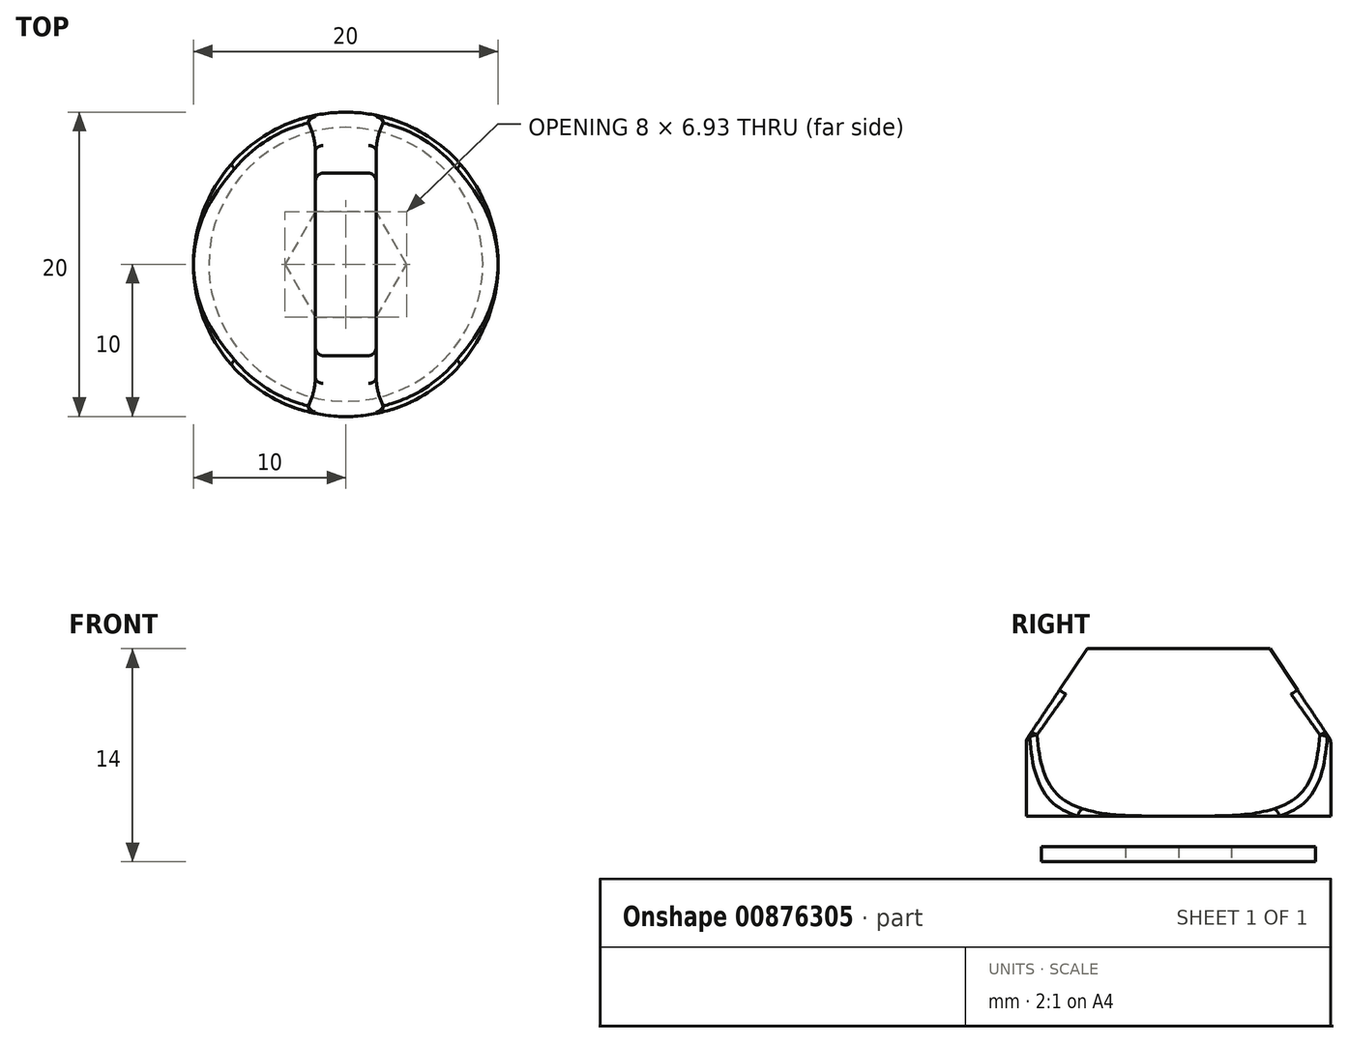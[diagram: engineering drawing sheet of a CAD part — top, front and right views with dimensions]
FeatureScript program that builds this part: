
annotation { "Feature Type Name" : "Feature", "Feature Type Description" : "" }
export const myFeature = defineFeature(function(context is Context, id is Id, definition is map)
    precondition{}
    {
        {
            var Q0;
            Q0=qCreatedBy(makeId("Top.planeOp"),FACE);
            var sketch = newSketch(context, id + "F0", { "sketchPlane" : qUnion([Q0])});
            skCircle(sketch, "E0", {"center": v(0, 0) * mm, "radius": 10 * mm});
            skCircle(sketch, "E1", {"center": v(0, 0) * mm, "radius": 9 * mm});
            skSolve(sketch);
        }
        {
            var Q0;
            Q0=makeQuery(id+"F0.imprint","IMPRINT",FACE,{"disambiguationData":[TD([[makeQuery(id+"F0.imprint","IMPRINT",EDGE,{"derivedFrom":sQuery(id+"F0.wireOp",EDGE,"E1")}),1.0]])]});
            var Q1;
            Q1=makeQuery(id+"F0.imprint","IMPRINT",FACE,{"disambiguationData":[TD([[makeQuery(id+"F0.imprint","IMPRINT",EDGE,{"derivedFrom":sQuery(id+"F0.wireOp",EDGE,"E0")}),1.0]])]});
            extrude(context, id + "F1", {"entities" : qUnion([Q0, Q1]), "depth" : 13 * mm, "offsetDistance" : 25 * mm});
        }
        {
            var Q0;
            Q0=makeQuery(id+"F0.imprint","IMPRINT",FACE,{"disambiguationData":[TD([[makeQuery(id+"F0.imprint","IMPRINT",EDGE,{"derivedFrom":sQuery(id+"F0.wireOp",EDGE,"E1")}),1.0]])]});
            extrude(context, id + "F2", {"entities" : qUnion([Q0]), "operationType" : NewBodyOperationType.ADD, "oppositeDirection" : true, "depth" : 1 * mm, "offsetDistance" : 25 * mm});
        }
        {
            var Q0;
            Q0=qCreatedBy(makeId("Front.planeOp"),FACE);
            var sketch = newSketch(context, id + "F3", { "sketchPlane" : qUnion([Q0])});
            skLineSegment(sketch, "E2.bottom", {"start": v(0, 0) * mm, "end": v(10, 0) * mm});
            skLineSegment(sketch, "E2.top", {"start": v(0, 13) * mm, "end": v(10, 13) * mm});
            skLineSegment(sketch, "E2.left", {"start": v(0, 0) * mm, "end": v(0, 13) * mm});
            skLineSegment(sketch, "E2.right", {"start": v(10, 0) * mm, "end": v(10, 13) * mm});
            skLineSegment(sketch, "E3.bottom", {"start": v(0, 0) * mm, "end": v(-10, 0) * mm});
            skLineSegment(sketch, "E3.top", {"start": v(0, 13) * mm, "end": v(-10, 13) * mm});
            skLineSegment(sketch, "E3.right", {"start": v(-10, 0) * mm, "end": v(-10, 13) * mm});
            skLineSegment(sketch, "E4.bottom", {"start": v(-10, 0) * mm, "end": v(10, 0) * mm});
            skLineSegment(sketch, "E4.top", {"start": v(-10, 2) * mm, "end": v(10, 2) * mm});
            skLineSegment(sketch, "E4.left", {"start": v(-10, 0) * mm, "end": v(-10, 2) * mm});
            skLineSegment(sketch, "E4.right", {"start": v(10, 0) * mm, "end": v(10, 2) * mm});
            skArc(sketch, "E5", {"start": v(2, 10) * mm, "mid": v(4.34, 4.34) * mm, "end": v(10, 2) * mm});
            skPoint(sketch, "E5.centerSnap0", {"position": v(10, 6.5) * mm});
            skArc(sketch, "E6", {"start": v(-10, 2) * mm, "mid": v(-4.34, 4.34) * mm, "end": v(-2, 10) * mm});
            skLineSegment(sketch, "E7", {"start": v(-2, 10) * mm, "end": v(-2, 13) * mm});
            skLineSegment(sketch, "E8", {"start": v(2, 10) * mm, "end": v(2, 13) * mm});
            skSolve(sketch);
        }
        {
            var Q0;
            {var subQ0=sQuery(id+"F3.wireOp",EDGE,"E3.right");Q0=makeQuery(id+"F3.imprint","IMPRINT",FACE,{"disambiguationData":[TD([[makeQuery(id+"F3.imprint","IMPRINT",EDGE,{"derivedFrom":subQ0}),-1.0]])]});}
            var Q1;
            {var subQ0=sQuery(id+"F3.wireOp",EDGE,"E2.right");Q1=makeQuery(id+"F3.imprint","IMPRINT",FACE,{"disambiguationData":[TD([[makeQuery(id+"F3.imprint","IMPRINT",EDGE,{"derivedFrom":subQ0}),1.0]])]});}
            extrude(context, id + "F4", {"entities" : qUnion([Q0, Q1]), "operationType" : NewBodyOperationType.REMOVE, "endBound" : BoundingType.SYMMETRIC, "oppositeDirection" : true, "depth" : 25 * mm, "offsetDistance" : 25 * mm});
        }
        {
            var Q0;
            Q0=qCreatedBy(makeId("Right.planeOp"),FACE);
            var sketch = newSketch(context, id + "F5", { "sketchPlane" : qUnion([Q0])});
            skLineSegment(sketch, "E9.bottom", {"start": v(0, 0) * mm, "end": v(10, 0) * mm});
            skLineSegment(sketch, "E9.top", {"start": v(0, 7) * mm, "end": v(10, 7) * mm});
            skLineSegment(sketch, "E9.left", {"start": v(0, 0) * mm, "end": v(0, 7) * mm});
            skLineSegment(sketch, "E9.right", {"start": v(10, 0) * mm, "end": v(10, 7) * mm});
            skLineSegment(sketch, "E10", {"start": v(0, 7) * mm, "end": v(0, 13) * mm});
            skLineSegment(sketch, "E11.bottom", {"start": v(0, 13) * mm, "end": v(6, 13) * mm});
            skLineSegment(sketch, "E11.top", {"start": v(0, 7) * mm, "end": v(6, 7) * mm});
            skLineSegment(sketch, "E11.left", {"start": v(0, 13) * mm, "end": v(0, 7) * mm});
            skLineSegment(sketch, "E11.right", {"start": v(6, 13) * mm, "end": v(6, 7) * mm});
            skLineSegment(sketch, "E12.bottom", {"start": v(0, 13) * mm, "end": v(-6, 13) * mm});
            skLineSegment(sketch, "E12.top", {"start": v(0, 7) * mm, "end": v(-6, 7) * mm});
            skLineSegment(sketch, "E12.right", {"start": v(-6, 13) * mm, "end": v(-6, 7) * mm});
            skLineSegment(sketch, "E13", {"start": v(6, 13) * mm, "end": v(10, 7) * mm});
            skLineSegment(sketch, "E14.bottom", {"start": v(0, 7) * mm, "end": v(-10, 7) * mm});
            skLineSegment(sketch, "E14.top", {"start": v(0, 0) * mm, "end": v(-10, 0) * mm});
            skLineSegment(sketch, "E14.left", {"start": v(0, 7) * mm, "end": v(0, 0) * mm});
            skLineSegment(sketch, "E14.right", {"start": v(-10, 7) * mm, "end": v(-10, 0) * mm});
            skLineSegment(sketch, "E15", {"start": v(-10, 7) * mm, "end": v(-6, 13) * mm});
            skLineSegment(sketch, "E16.bottom", {"start": v(-6, 7) * mm, "end": v(-10, 7) * mm});
            skLineSegment(sketch, "E16.top", {"start": v(-6, 13) * mm, "end": v(-10, 13) * mm});
            skLineSegment(sketch, "E16.left", {"start": v(-6, 7) * mm, "end": v(-6, 13) * mm});
            skLineSegment(sketch, "E16.right", {"start": v(-10, 7) * mm, "end": v(-10, 13) * mm});
            skLineSegment(sketch, "E17.bottom", {"start": v(6, 13) * mm, "end": v(10, 13) * mm});
            skLineSegment(sketch, "E17.top", {"start": v(6, 7) * mm, "end": v(10, 7) * mm});
            skLineSegment(sketch, "E17.right", {"start": v(10, 13) * mm, "end": v(10, 7) * mm});
            skSolve(sketch);
        }
        {
            var Q0;
            Q0=makeQuery(id+"F5.imprint","IMPRINT",FACE,{"disambiguationData":[TD([[makeQuery(id+"F5.imprint","IMPRINT",EDGE,{"derivedFrom":sQuery(id+"F5.wireOp",EDGE,"E15")}),1.0]])]});
            var Q1;
            Q1=makeQuery(id+"F5.imprint","IMPRINT",FACE,{"disambiguationData":[TD([[makeQuery(id+"F5.imprint","IMPRINT",EDGE,{"derivedFrom":sQuery(id+"F5.wireOp",EDGE,"E13")}),1.0]])]});
            extrude(context, id + "F6", {"entities" : qUnion([Q0, Q1]), "operationType" : NewBodyOperationType.REMOVE, "endBound" : BoundingType.SYMMETRIC, "oppositeDirection" : true, "depth" : 25 * mm, "offsetDistance" : 25 * mm});
        }
        {
            var Q0;
            Q0=makeQuery(id+"F4.boolean.opBoolean","COPY",EDGE,{"derivedFrom":makeQuery(id+"F4.opExtrude","SWEPT_EDGE",EDGE,{"disambiguationData":[OSD([sQuery(id+"F3.wireOp",EDGE,"E3.top"),sQuery(id+"F3.wireOp",EDGE,"E7")])]})});
            var Q1;
            Q1=makeQuery(id+"F4.boolean.opBoolean","COPY",EDGE,{"derivedFrom":makeQuery(id+"F4.opExtrude","SWEPT_EDGE",EDGE,{"disambiguationData":[OSD([sQuery(id+"F3.wireOp",EDGE,"E2.top"),sQuery(id+"F3.wireOp",EDGE,"E8")])]})});
            var Q2;
            Q2=makeQuery(id+"F6.boolean.opBoolean","COPY",EDGE,{"derivedFrom":makeQuery(id+"F6.opExtrude","SWEPT_EDGE",EDGE,{"disambiguationData":[OSD([sQuery(id+"F5.wireOp",EDGE,"E12.bottom"),sQuery(id+"F5.wireOp",EDGE,"E15"),sQuery(id+"F5.wireOp",EDGE,"E16.top"),sQuery(id+"F5.wireOp",EDGE,"E16.left")])]})});
            var Q3;
            Q3=makeQuery(id+"F6.boolean.opBoolean","INTERSECT",EDGE,{"derivedFrom":[makeQuery(id+"F4.boolean.opBoolean","COPY",FACE,{"derivedFrom":makeQuery(id+"F4.opExtrude","SWEPT_FACE",FACE,{"disambiguationData":[OSD([sQuery(id+"F3.wireOp",EDGE,"E8")])]})}),makeQuery(id+"F6.opExtrude","SWEPT_FACE",FACE,{"disambiguationData":[OSD([sQuery(id+"F5.wireOp",EDGE,"E15")])]})]});
            var Q4;
            Q4=makeQuery(id+"F6.boolean.opBoolean","INTERSECT",EDGE,{"derivedFrom":[makeQuery(id+"F4.boolean.opBoolean","COPY",FACE,{"derivedFrom":makeQuery(id+"F4.opExtrude","SWEPT_FACE",FACE,{"disambiguationData":[OSD([sQuery(id+"F3.wireOp",EDGE,"E7")])]})}),makeQuery(id+"F6.opExtrude","SWEPT_FACE",FACE,{"disambiguationData":[OSD([sQuery(id+"F5.wireOp",EDGE,"E15")])]})]});
            var Q5;
            Q5=makeQuery(id+"F6.boolean.opBoolean","INTERSECT",EDGE,{"derivedFrom":[makeQuery(id+"F4.boolean.opBoolean","COPY",FACE,{"derivedFrom":makeQuery(id+"F4.opExtrude","SWEPT_FACE",FACE,{"disambiguationData":[OSD([sQuery(id+"F3.wireOp",EDGE,"E5")])]})}),makeQuery(id+"F6.opExtrude","SWEPT_FACE",FACE,{"disambiguationData":[OSD([sQuery(id+"F5.wireOp",EDGE,"E15")])]})]});
            var Q6;
            Q6=makeQuery(id+"F6.boolean.opBoolean","INTERSECT",EDGE,{"derivedFrom":[makeQuery(id+"F4.boolean.opBoolean","COPY",FACE,{"derivedFrom":makeQuery(id+"F4.opExtrude","SWEPT_FACE",FACE,{"disambiguationData":[OSD([sQuery(id+"F3.wireOp",EDGE,"E6")])]})}),makeQuery(id+"F6.opExtrude","SWEPT_FACE",FACE,{"disambiguationData":[OSD([sQuery(id+"F5.wireOp",EDGE,"E15")])]})]});
            var Q7;
            Q7=makeQuery(id+"F6.boolean.opBoolean","INTERSECT",EDGE,{"derivedFrom":[makeQuery(id+"F1.opExtrude","SWEPT_FACE",FACE,{"disambiguationData":[OSD([sQuery(id+"F0.wireOp",EDGE,"E0")])]}),makeQuery(id+"F6.opExtrude","SWEPT_FACE",FACE,{"disambiguationData":[OSD([sQuery(id+"F5.wireOp",EDGE,"E15")])]})]});
            var Q8;
            Q8=makeQuery(id+"F6.boolean.opBoolean","COPY",EDGE,{"derivedFrom":makeQuery(id+"F6.opExtrude","SWEPT_EDGE",EDGE,{"disambiguationData":[OSD([sQuery(id+"F5.wireOp",EDGE,"E11.bottom"),sQuery(id+"F5.wireOp",EDGE,"E13"),sQuery(id+"F5.wireOp",EDGE,"E17.bottom"),sQuery(id+"F5.wireOp",EDGE,"E11.right")])]})});
            var Q9;
            Q9=makeQuery(id+"F6.boolean.opBoolean","INTERSECT",EDGE,{"derivedFrom":[makeQuery(id+"F4.boolean.opBoolean","COPY",FACE,{"derivedFrom":makeQuery(id+"F4.opExtrude","SWEPT_FACE",FACE,{"disambiguationData":[OSD([sQuery(id+"F3.wireOp",EDGE,"E7")])]})}),makeQuery(id+"F6.opExtrude","SWEPT_FACE",FACE,{"disambiguationData":[OSD([sQuery(id+"F5.wireOp",EDGE,"E13")])]})]});
            var Q10;
            Q10=makeQuery(id+"F6.boolean.opBoolean","INTERSECT",EDGE,{"derivedFrom":[makeQuery(id+"F4.boolean.opBoolean","COPY",FACE,{"derivedFrom":makeQuery(id+"F4.opExtrude","SWEPT_FACE",FACE,{"disambiguationData":[OSD([sQuery(id+"F3.wireOp",EDGE,"E6")])]})}),makeQuery(id+"F6.opExtrude","SWEPT_FACE",FACE,{"disambiguationData":[OSD([sQuery(id+"F5.wireOp",EDGE,"E13")])]})]});
            var Q11;
            Q11=makeQuery(id+"F6.boolean.opBoolean","INTERSECT",EDGE,{"derivedFrom":[makeQuery(id+"F4.boolean.opBoolean","COPY",FACE,{"derivedFrom":makeQuery(id+"F4.opExtrude","SWEPT_FACE",FACE,{"disambiguationData":[OSD([sQuery(id+"F3.wireOp",EDGE,"E5")])]})}),makeQuery(id+"F6.opExtrude","SWEPT_FACE",FACE,{"disambiguationData":[OSD([sQuery(id+"F5.wireOp",EDGE,"E13")])]})]});
            var Q12;
            Q12=makeQuery(id+"F6.boolean.opBoolean","INTERSECT",EDGE,{"derivedFrom":[makeQuery(id+"F4.boolean.opBoolean","COPY",FACE,{"derivedFrom":makeQuery(id+"F4.opExtrude","SWEPT_FACE",FACE,{"disambiguationData":[OSD([sQuery(id+"F3.wireOp",EDGE,"E8")])]})}),makeQuery(id+"F6.opExtrude","SWEPT_FACE",FACE,{"disambiguationData":[OSD([sQuery(id+"F5.wireOp",EDGE,"E13")])]})]});
            var Q13;
            Q13=makeQuery(id+"F6.boolean.opBoolean","INTERSECT",EDGE,{"derivedFrom":[makeQuery(id+"F1.opExtrude","SWEPT_FACE",FACE,{"disambiguationData":[OSD([sQuery(id+"F0.wireOp",EDGE,"E0")])]}),makeQuery(id+"F6.opExtrude","SWEPT_FACE",FACE,{"disambiguationData":[OSD([sQuery(id+"F5.wireOp",EDGE,"E13")])]})]});
            var Q14;
            Q14=makeQuery(id+"F4.boolean.opBoolean","INTERSECT",EDGE,{"derivedFrom":[makeQuery(id+"F1.opExtrude","SWEPT_FACE",FACE,{"disambiguationData":[OSD([sQuery(id+"F0.wireOp",EDGE,"E0")])]}),makeQuery(id+"F4.opExtrude","SWEPT_FACE",FACE,{"disambiguationData":[OSD([sQuery(id+"F3.wireOp",EDGE,"E5")])]})]});
            var Q15;
            Q15=makeQuery(id+"F4.boolean.opBoolean","INTERSECT",EDGE,{"derivedFrom":[makeQuery(id+"F1.opExtrude","SWEPT_FACE",FACE,{"disambiguationData":[OSD([sQuery(id+"F0.wireOp",EDGE,"E0")])]}),makeQuery(id+"F4.opExtrude","SWEPT_FACE",FACE,{"disambiguationData":[OSD([sQuery(id+"F3.wireOp",EDGE,"E6")])]})]});
            fillet(context, id + "F7", {"entities" : qUnion([Q0, Q1, Q2, Q3, Q4, Q5, Q6, Q7, Q8, Q9, Q10, Q11, Q12, Q13, Q14, Q15]), "radius" : 0.5 * mm, "tangentPropagation" : true, "allowEdgeOverflow" : false});
        }
        {
            var Q0;
            Q0=makeQuery(id+"F2.opExtrude","CAP_FACE",FACE,{"disambiguationData":[OSD([sQuery(id+"F0.wireOp",EDGE,"E1")])],"isStart":false});
            var sketch = newSketch(context, id + "F8", { "sketchPlane" : qUnion([Q0])});
            skCircle(sketch, "E18", {"center": v(0, 0) * mm, "radius": 4 * mm});
            skCircle(sketch, "E19.cCircle", {"center": v(0, 0) * mm, "radius": 4 * mm, "construction": true});
            skLineSegment(sketch, "E19.0", {"start": v(4, 0) * mm, "end": v(2, -3.46) * mm});
            skLineSegment(sketch, "E19.1", {"start": v(2, -3.46) * mm, "end": v(-2, -3.46) * mm});
            skLineSegment(sketch, "E19.2", {"start": v(-2, -3.46) * mm, "end": v(-4, 0) * mm});
            skLineSegment(sketch, "E19.3", {"start": v(-4, 0) * mm, "end": v(-2, 3.46) * mm});
            skLineSegment(sketch, "E19.4", {"start": v(-2, 3.46) * mm, "end": v(2, 3.46) * mm});
            skLineSegment(sketch, "E19.5", {"start": v(2, 3.46) * mm, "end": v(4, 0) * mm});
            skSolve(sketch);
        }
        {
            var Q0;
            Q0=makeQuery(id+"F8.imprint","IMPRINT",FACE,{"disambiguationData":[TD([[makeQuery(id+"F8.imprint","IMPRINT",EDGE,{"derivedFrom":sQuery(id+"F8.wireOp",EDGE,"E19.0")}),-1.0]])]});
            extrude(context, id + "F9", {"entities" : qUnion([Q0]), "operationType" : NewBodyOperationType.REMOVE, "oppositeDirection" : true, "depth" : 3 * mm, "offsetDistance" : 25 * mm});
        }
    });
